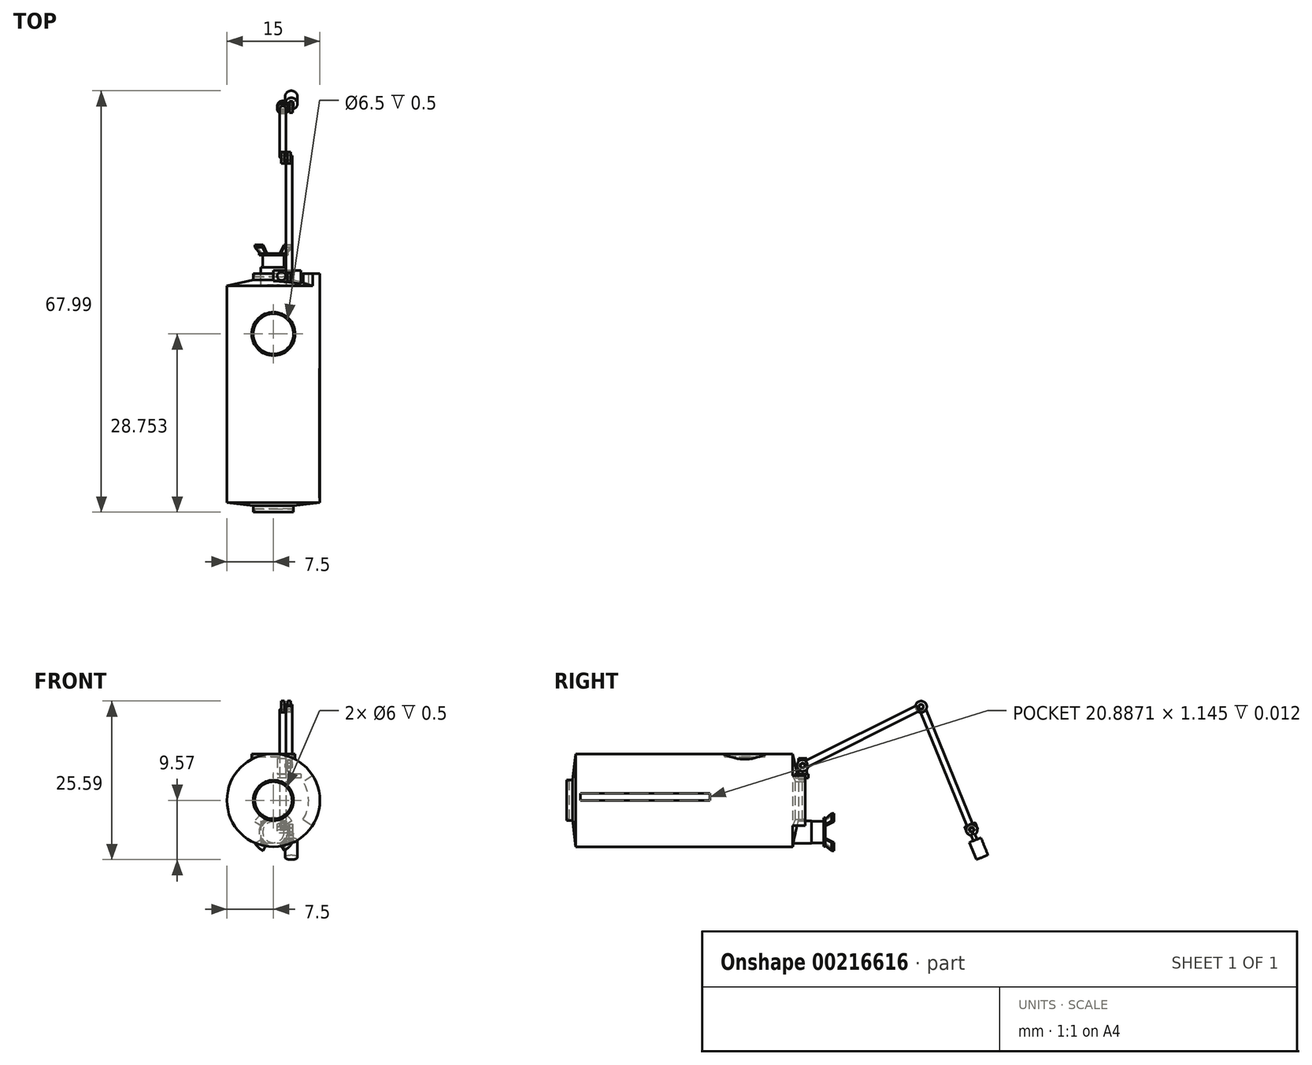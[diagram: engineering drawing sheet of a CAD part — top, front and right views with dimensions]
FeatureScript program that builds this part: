
annotation { "Feature Type Name" : "Feature", "Feature Type Description" : "" }
export const myFeature = defineFeature(function(context is Context, id is Id, definition is map)
    precondition{}
    {
        {
            var Q0;
            Q0=qCreatedBy(makeId("Front.planeOp"),FACE);
            var sketch = newSketch(context, id + "F0", { "sketchPlane" : qUnion([Q0])});
            skCircle(sketch, "E0", {"center": v(0, 0) * mm, "radius": 3.25 * mm});
            skSolve(sketch);
        }
        {
            var Q0;
            Q0=qCreatedBy(makeId("Front.planeOp"),FACE);
            cPlane(context, id + "F1", {"entities" : qUnion([Q0]), "cplaneType" : CPlaneType.OFFSET, "offset" : .5 * mm, "oppositeDirection" : true, "width" : 150 * mm, "height" : 150 * mm});
        }
        {
            var Q0;
            Q0=qCreatedBy(id+"F1.planeOp",FACE);
            var sketch = newSketch(context, id + "F2", { "sketchPlane" : qUnion([Q0])});
            skCircle(sketch, "E1", {"center": v(0, 0) * mm, "radius": 7.5 * mm});
            skSolve(sketch);
        }
        {
            var Q0;
            Q0=makeQuery(id+"F0.imprint","IMPRINT",FACE,{"disambiguationData":[TD([[makeQuery(id+"F0.imprint","IMPRINT",EDGE,{"derivedFrom":sQuery(id+"F0.wireOp",EDGE,"E0")}),1.0]])]});
            var Q1;
            Q1=makeQuery(id+"F2.imprint","IMPRINT",FACE,{"disambiguationData":[TD([[makeQuery(id+"F2.imprint","IMPRINT",EDGE,{"derivedFrom":sQuery(id+"F2.wireOp",EDGE,"E1")}),1.0]])]});
            loft(context, id + "F3", {"sheetProfilesArray" : [{ "sheetProfileEntities" : qUnion([Q0]) }, { "sheetProfileEntities" : qUnion([Q1]) }]});
        }
        {
            var Q0;
            Q0=makeQuery(id+"F3.opLoft","CAP_FACE",FACE,{"disambiguationData":[OSD([makeQuery(id+"F0.imprint","IMPRINT",FACE,{"disambiguationData":[TD([[makeQuery(id+"F0.imprint","IMPRINT",EDGE,{"derivedFrom":sQuery(id+"F0.wireOp",EDGE,"E0")}),1.0]])]})])],"isStart":true});
            extrude(context, id + "F4", {"entities" : qUnion([Q0]), "operationType" : NewBodyOperationType.ADD, "depth" : 1 * mm});
        }
        {
            var Q0;
            Q0=makeQuery(id+"F4.opExtrude","CAP_FACE",FACE,{"disambiguationData":[OSD([makeQuery(id+"F0.imprint","IMPRINT",FACE,{"disambiguationData":[TD([[makeQuery(id+"F0.imprint","IMPRINT",EDGE,{"derivedFrom":sQuery(id+"F0.wireOp",EDGE,"E0")}),1.0]])]})])],"isStart":false});
            var sketch = newSketch(context, id + "F5", { "sketchPlane" : qUnion([Q0])});
            skCircle(sketch, "E2", {"center": v(0, 0) * mm, "radius": 3 * mm});
            skSolve(sketch);
        }
        {
            var Q0;
            Q0=makeQuery(id+"F5.imprint","IMPRINT",FACE,{"disambiguationData":[TD([[makeQuery(id+"F5.imprint","IMPRINT",EDGE,{"derivedFrom":sQuery(id+"F5.wireOp",EDGE,"E2")}),1.0]])]});
            extrude(context, id + "F6", {"entities" : qUnion([Q0]), "operationType" : NewBodyOperationType.REMOVE, "oppositeDirection" : true, "depth" : .5 * mm});
        }
        {
            var Q0;
            Q0=makeQuery(id+"F3.opLoft","CAP_FACE",FACE,{"disambiguationData":[OSD([makeQuery(id+"F2.imprint","IMPRINT",FACE,{"disambiguationData":[TD([[makeQuery(id+"F2.imprint","IMPRINT",EDGE,{"derivedFrom":sQuery(id+"F2.wireOp",EDGE,"E1")}),1.0]])]})])],"isStart":true});
            extrude(context, id + "F7", {"entities" : qUnion([Q0]), "operationType" : NewBodyOperationType.ADD, "depth" : 35 * mm});
        }
        {
            var Q0;
            Q0=qCreatedBy(makeId("Right.planeOp"),FACE);
            cPlane(context, id + "F8", {"entities" : qUnion([Q0]), "cplaneType" : CPlaneType.OFFSET, "offset" : 7.5 * mm, "width" : 150 * mm, "height" : 150 * mm});
        }
        {
            var Q0;
            Q0=qCreatedBy(id+"F8.planeOp",FACE);
            var sketch = newSketch(context, id + "F9", { "sketchPlane" : qUnion([Q0])});
            skLineSegment(sketch, "E3.bottom", {"start": v(1.27, 0) * mm, "end": v(22.15, 0) * mm});
            skLineSegment(sketch, "E3.top", {"start": v(1.27, 1.15) * mm, "end": v(22.15, 1.15) * mm});
            skLineSegment(sketch, "E3.left", {"start": v(1.27, 0) * mm, "end": v(1.27, 1.15) * mm});
            skLineSegment(sketch, "E3.right", {"start": v(22.15, 0) * mm, "end": v(22.15, 1.15) * mm});
            skSolve(sketch);
        }
        {
            var Q0;
            Q0=makeQuery(id+"F9.imprint","IMPRINT",FACE,{"disambiguationData":[TD([[makeQuery(id+"F9.imprint","IMPRINT",EDGE,{"derivedFrom":sQuery(id+"F9.wireOp",EDGE,"E3.bottom")}),1.0]])]});
            extrude(context, id + "F10", {"entities" : qUnion([Q0]), "operationType" : NewBodyOperationType.REMOVE, "oppositeDirection" : true, "depth" : .1 * mm});
        }
        {
            var Q0;
            Q0=qCreatedBy(id+"F1.planeOp",FACE);
            cPlane(context, id + "F11", {"entities" : qUnion([Q0]), "cplaneType" : CPlaneType.OFFSET, "offset" : 36 * mm, "oppositeDirection" : true, "width" : 150 * mm, "height" : 150 * mm});
        }
        {
            var Q0;
            Q0=qCreatedBy(id+"F11.planeOp",FACE);
            var sketch = newSketch(context, id + "F12", { "sketchPlane" : qUnion([Q0])});
            skCircle(sketch, "E4", {"center": v(0, 0) * mm, "radius": 3.25 * mm});
            skSolve(sketch);
        }
        {
            var Q1;
            Q1=makeQuery(id+"F7.opExtrude","CAP_FACE",FACE,{"disambiguationData":[OSD([makeQuery(id+"F2.imprint","IMPRINT",FACE,{"disambiguationData":[TD([[makeQuery(id+"F2.imprint","IMPRINT",EDGE,{"derivedFrom":sQuery(id+"F2.wireOp",EDGE,"E1")}),1.0]])]})])],"isStart":false});
            var Q2;
            Q2=makeQuery(id+"F12.imprint","IMPRINT",FACE,{"disambiguationData":[TD([[makeQuery(id+"F12.imprint","IMPRINT",EDGE,{"derivedFrom":sQuery(id+"F12.wireOp",EDGE,"E4")}),1.0]])]});
            loft(context, id + "F13", {"operationType" : NewBodyOperationType.ADD, "sheetProfilesArray" : [{ "sheetProfileEntities" : qUnion([Q1]) }, { "sheetProfileEntities" : qUnion([Q2]) }]});
        }
        {
            var Q0;
            Q0=makeQuery(id+"F13.opLoft","CAP_FACE",FACE,{"disambiguationData":[OSD([makeQuery(id+"F12.imprint","IMPRINT",FACE,{"disambiguationData":[TD([[makeQuery(id+"F12.imprint","IMPRINT",EDGE,{"derivedFrom":sQuery(id+"F12.wireOp",EDGE,"E4")}),1.0]])]})])],"isStart":true});
            extrude(context, id + "F14", {"entities" : qUnion([Q0]), "operationType" : NewBodyOperationType.ADD, "depth" : 1 * mm});
        }
        {
            var Q0;
            Q0=qCreatedBy(id+"F11.planeOp",FACE);
            var sketch = newSketch(context, id + "F15", { "sketchPlane" : qUnion([Q0])});
            skLineSegment(sketch, "E5", {"start": v(0, 0) * mm, "end": v(0, -7.48) * mm});
            skLineSegment(sketch, "E6", {"start": v(0, -7.48) * mm, "end": v(0, -3.26) * mm});
            skLineSegment(sketch, "E7.bottom", {"start": v(2.05, -3.32) * mm, "end": v(-2.05, -3.32) * mm});
            skLineSegment(sketch, "E7.top", {"start": v(2.05, -6.95) * mm, "end": v(-2.05, -6.95) * mm});
            skLineSegment(sketch, "E7.left", {"start": v(2.05, -3.32) * mm, "end": v(2.05, -6.95) * mm});
            skLineSegment(sketch, "E7.right", {"start": v(-2.05, -3.32) * mm, "end": v(-2.05, -6.95) * mm});
            skPoint(sketch, "E7.middle", {"position": v(0, -5.13) * mm});
            skSolve(sketch);
        }
        {
            var Q0;
            {var subQ5=sQuery(id+"F15.wireOp",EDGE,"E7.left");Q0=makeQuery(id+"F15.imprint","IMPRINT",FACE,{"disambiguationData":[TD([[makeQuery(id+"F15.imprint","IMPRINT",EDGE,{"derivedFrom":subQ5}),-1.0]])]});}
            var Q1;
            {var subQ5=sQuery(id+"F15.wireOp",EDGE,"E7.right");Q1=makeQuery(id+"F15.imprint","IMPRINT",FACE,{"disambiguationData":[TD([[makeQuery(id+"F15.imprint","IMPRINT",EDGE,{"derivedFrom":subQ5}),1.0]])]});}
            extrude(context, id + "F16", {"entities" : qUnion([Q0, Q1]), "operationType" : NewBodyOperationType.ADD, "depth" : 3 * mm, "hasSecondDirection" : true, "secondDirectionOppositeDirection" : true, "secondDirectionDepth" : 2 * mm});
        }
        {
            var Q0;
            Q0=qCreatedBy(id+"F11.planeOp",FACE);
            var sketch = newSketch(context, id + "F17", { "sketchPlane" : qUnion([Q0])});
            skCircle(sketch, "E8", {"center": v(0, 0) * mm, "radius": 7.5 * mm});
            skLineSegment(sketch, "E9", {"start": v(4.81, 3) * mm, "end": v(6.36, 3.97) * mm});
            skLineSegment(sketch, "E10", {"start": v(6.3, -4.05) * mm, "end": v(4.78, -3.07) * mm});
            skArc(sketch, "E11", {"start": v(4.78, -3.07) * mm, "mid": v(5.68, -0.04) * mm, "end": v(4.81, 3) * mm});
            skSolve(sketch);
        }
        {
            var Q0;
            {var subQ0=sQuery(id+"F17.wireOp",EDGE,"E9");Q0=makeQuery(id+"F17.imprint","IMPRINT",FACE,{"disambiguationData":[TD([[makeQuery(id+"F17.imprint","IMPRINT",EDGE,{"derivedFrom":subQ0}),-1.0]])]});}
            extrude(context, id + "F18", {"entities" : qUnion([Q0]), "operationType" : NewBodyOperationType.ADD, "depth" : 2 * mm, "hasSecondDirection" : true, "secondDirectionOppositeDirection" : true, "secondDirectionDepth" : 1 * mm});
        }
        {
            var Q0;
            Q0=qCreatedBy(id+"F11.planeOp",FACE);
            var sketch = newSketch(context, id + "F19", { "sketchPlane" : qUnion([Q0])});
            skLineSegment(sketch, "E12.bottom", {"start": v(4.44, 4.25) * mm, "end": v(0, 4.25) * mm});
            skLineSegment(sketch, "E12.top", {"start": v(4.44, 3.61) * mm, "end": v(0, 3.61) * mm});
            skLineSegment(sketch, "E12.left", {"start": v(4.44, 4.25) * mm, "end": v(4.44, 3.61) * mm});
            skLineSegment(sketch, "E12.right", {"start": v(0, 4.25) * mm, "end": v(0, 3.61) * mm});
            skSolve(sketch);
        }
        {
            var Q0;
            Q0=makeQuery(id+"F19.imprint","IMPRINT",FACE,{"disambiguationData":[TD([[makeQuery(id+"F19.imprint","IMPRINT",EDGE,{"derivedFrom":sQuery(id+"F19.wireOp",EDGE,"E12.bottom")}),1.0]])]});
            extrude(context, id + "F20", {"entities" : qUnion([Q0]), "operationType" : NewBodyOperationType.ADD, "depth" : 2 * mm, "hasSecondDirection" : true, "secondDirectionOppositeDirection" : true, "secondDirectionDepth" : 1.5 * mm});
        }
        {
            var Q0;
            Q0=makeQuery(id+"F20.opExtrude","SWEPT_FACE",FACE,{"disambiguationData":[OSD([sQuery(id+"F19.wireOp",EDGE,"E12.bottom")])]});
            var sketch = newSketch(context, id + "F21", { "sketchPlane" : qUnion([Q0])});
            skCircle(sketch, "E13", {"center": v(1.29, 37.08) * mm, "radius": 0.67 * mm});
            skSolve(sketch);
        }
        {
            var Q0;
            Q0=makeQuery(id+"F21.imprint","IMPRINT",FACE,{"disambiguationData":[TD([[makeQuery(id+"F21.imprint","IMPRINT",EDGE,{"derivedFrom":sQuery(id+"F21.wireOp",EDGE,"E13")}),1.0]])]});
            extrude(context, id + "F22", {"entities" : qUnion([Q0]), "operationType" : NewBodyOperationType.ADD, "depth" : 2.5 * mm});
        }
        {
            var Q0;
            Q0=qCreatedBy(makeId("Right.planeOp"),FACE);
            cPlane(context, id + "F23", {"entities" : qUnion([Q0]), "cplaneType" : CPlaneType.OFFSET, "offset" : 2 * mm, "width" : 150 * mm, "height" : 150 * mm});
        }
        {
            var Q0;
            Q0=qCreatedBy(id+"F23.planeOp",FACE);
            var sketch = newSketch(context, id + "F24", { "sketchPlane" : qUnion([Q0])});
            skCircle(sketch, "E14", {"center": v(37.1, 5.6) * mm, "radius": 0.33 * mm});
            skSolve(sketch);
        }
        {
            var Q0;
            Q0=makeQuery(id+"F24.imprint","IMPRINT",FACE,{"disambiguationData":[TD([[makeQuery(id+"F24.imprint","IMPRINT",EDGE,{"derivedFrom":sQuery(id+"F24.wireOp",EDGE,"E14")}),1.0]])]});
            extrude(context, id + "F25", {"entities" : qUnion([Q0]), "operationType" : NewBodyOperationType.ADD, "depth" : 1 * mm, "hasSecondDirection" : true, "secondDirectionOppositeDirection" : true, "secondDirectionDepth" : 1 * mm});
        }
        {
            var Q0;
            Q0=qCreatedBy(id+"F23.planeOp",FACE);
            cPlane(context, id + "F26", {"entities" : qUnion([Q0]), "cplaneType" : CPlaneType.OFFSET, "offset" : .5 * mm, "width" : 150 * mm, "height" : 150 * mm});
        }
        {
            var Q0;
            Q0=qCreatedBy(id+"F26.planeOp",FACE);
            var sketch = newSketch(context, id + "F27", { "sketchPlane" : qUnion([Q0])});
            skCircle(sketch, "E15", {"center": v(37.1, 5.61) * mm, "radius": 0.92 * mm});
            skCircle(sketch, "E16", {"center": v(37.1, 5.61) * mm, "radius": 0.4 * mm});
            skSolve(sketch);
        }
        {
            var Q0;
            Q0=makeQuery(id+"F27.imprint","IMPRINT",FACE,{"disambiguationData":[TD([[makeQuery(id+"F27.imprint","IMPRINT",EDGE,{"derivedFrom":sQuery(id+"F27.wireOp",EDGE,"E15")}),1.0]])]});
            extrude(context, id + "F28", {"entities" : qUnion([Q0]), "depth" : .25 * mm, "hasSecondDirection" : true, "secondDirectionOppositeDirection" : true, "secondDirectionDepth" : .25 * mm});
        }
        {
            var Q0;
            Q0=qCreatedBy(id+"F26.planeOp",FACE);
            var sketch = newSketch(context, id + "F29", { "sketchPlane" : qUnion([Q0])});
            skLineSegment(sketch, "E17", {"start": v(37.13, 5.58) * mm, "end": v(37.8, 5.91) * mm});
            skLineSegment(sketch, "E18", {"start": v(37.8, 5.91) * mm, "end": v(37.57, 6.36) * mm});
            skLineSegment(sketch, "E19", {"start": v(37.8, 5.91) * mm, "end": v(38.01, 5.47) * mm});
            skLineSegment(sketch, "E20", {"start": v(37.57, 6.36) * mm, "end": v(55.46, 15.3) * mm});
            skLineSegment(sketch, "E21", {"start": v(38.01, 5.47) * mm, "end": v(55.9, 14.41) * mm});
            skLineSegment(sketch, "E22", {"start": v(55.9, 14.41) * mm, "end": v(55.46, 15.3) * mm});
            skSolve(sketch);
        }
        {
            var Q0;
            Q0=makeQuery(id+"F29.imprint","IMPRINT",FACE,{"disambiguationData":[TD([[makeQuery(id+"F29.imprint","IMPRINT",EDGE,{"derivedFrom":sQuery(id+"F29.wireOp",EDGE,"E18")}),-1.0]])]});
            extrude(context, id + "F30", {"entities" : qUnion([Q0]), "operationType" : NewBodyOperationType.ADD, "oppositeDirection" : true, "depth" : .5 * mm, "hasSecondDirection" : true, "secondDirectionOppositeDirection" : false, "secondDirectionDepth" : .5 * mm});
        }
        {
            var Q0;
            Q0=makeQuery(id+"F30.opExtrude","CAP_EDGE",EDGE,{"disambiguationData":[OSD([sQuery(id+"F29.wireOp",EDGE,"E20")])],"isStart":true});
            var Q1;
            Q1=makeQuery(id+"F30.opExtrude","CAP_EDGE",EDGE,{"disambiguationData":[OSD([sQuery(id+"F29.wireOp",EDGE,"E21")])],"isStart":true});
            var Q2;
            Q2=makeQuery(id+"F30.opExtrude","CAP_EDGE",EDGE,{"disambiguationData":[OSD([sQuery(id+"F29.wireOp",EDGE,"E20")])],"isStart":false});
            var Q3;
            Q3=makeQuery(id+"F30.opExtrude","CAP_EDGE",EDGE,{"disambiguationData":[OSD([sQuery(id+"F29.wireOp",EDGE,"E21")])],"isStart":false});
            fillet(context, id + "F31", {"entities" : qUnion([Q0, Q1, Q2, Q3]), "radius" : .3 * mm, "tangentPropagation" : true, "allowEdgeOverflow" : false});
        }
        {
            var Q0;
            Q0=qCreatedBy(id+"F26.planeOp",FACE);
            var sketch = newSketch(context, id + "F32", { "sketchPlane" : qUnion([Q0])});
            skCircle(sketch, "E23", {"center": v(56.2, 15.1) * mm, "radius": 0.92 * mm});
            skCircle(sketch, "E24", {"center": v(56.2, 15.1) * mm, "radius": 0.4 * mm});
            skSolve(sketch);
        }
        {
            var Q0;
            Q0=makeQuery(id+"F32.imprint","IMPRINT",FACE,{"disambiguationData":[TD([[makeQuery(id+"F32.imprint","IMPRINT",EDGE,{"derivedFrom":sQuery(id+"F32.wireOp",EDGE,"E23")}),1.0]])]});
            extrude(context, id + "F33", {"entities" : qUnion([Q0]), "operationType" : NewBodyOperationType.ADD, "depth" : .25 * mm, "hasSecondDirection" : true, "secondDirectionOppositeDirection" : true, "secondDirectionDepth" : .25 * mm});
        }
        {
            var Q0;
            Q0=qCreatedBy(id+"F23.planeOp",FACE);
            var sketch = newSketch(context, id + "F34", { "sketchPlane" : qUnion([Q0])});
            skLineSegment(sketch, "E25", {"start": v(55.8, 15.1) * mm, "end": v(56.6, 15.1) * mm});
            skLineSegment(sketch, "E26", {"start": v(56.2, 15.5) * mm, "end": v(56.2, 14.7) * mm});
            skCircle(sketch, "E27", {"center": v(56.2, 15.1) * mm, "radius": 0.36 * mm});
            skSolve(sketch);
        }
        {
            var Q0;
            {var subQ0=sQuery(id+"F34.wireOp",EDGE,"E27");var subQ1=sQuery(id+"F34.wireOp",EDGE,"E25");var subQ2=makeQuery(id+"F34.imprint","INTERSECT",VERTEX,{"disambiguationData":[OD(1.0)],"derivedFrom":[subQ1,subQ0]});Q0=makeQuery(id+"F34.imprint","IMPRINT",FACE,{"disambiguationData":[TD([[makeQuery(id+"F34.imprint","IMPRINT",EDGE,{"disambiguationData":[TD([[subQ2,1.0]])],"derivedFrom":subQ1}),-1.0]])]});}
            var Q1;
            {var subQ0=sQuery(id+"F34.wireOp",EDGE,"E27");var subQ1=sQuery(id+"F34.wireOp",EDGE,"E25");var subQ2=makeQuery(id+"F34.imprint","INTERSECT",VERTEX,{"disambiguationData":[OD(0.0)],"derivedFrom":[subQ1,subQ0]});Q1=makeQuery(id+"F34.imprint","IMPRINT",FACE,{"disambiguationData":[TD([[makeQuery(id+"F34.imprint","IMPRINT",EDGE,{"disambiguationData":[TD([[subQ2,-1.0]])],"derivedFrom":subQ1}),-1.0]])]});}
            var Q2;
            {var subQ0=sQuery(id+"F34.wireOp",EDGE,"E27");var subQ1=sQuery(id+"F34.wireOp",EDGE,"E25");var subQ2=makeQuery(id+"F34.imprint","INTERSECT",VERTEX,{"disambiguationData":[OD(1.0)],"derivedFrom":[subQ1,subQ0]});Q2=makeQuery(id+"F34.imprint","IMPRINT",FACE,{"disambiguationData":[TD([[makeQuery(id+"F34.imprint","IMPRINT",EDGE,{"disambiguationData":[TD([[subQ2,1.0]])],"derivedFrom":subQ1}),1.0]])]});}
            var Q3;
            {var subQ0=sQuery(id+"F34.wireOp",EDGE,"E27");var subQ1=sQuery(id+"F34.wireOp",EDGE,"E25");var subQ2=makeQuery(id+"F34.imprint","INTERSECT",VERTEX,{"disambiguationData":[OD(0.0)],"derivedFrom":[subQ1,subQ0]});Q3=makeQuery(id+"F34.imprint","IMPRINT",FACE,{"disambiguationData":[TD([[makeQuery(id+"F34.imprint","IMPRINT",EDGE,{"disambiguationData":[TD([[subQ2,-1.0]])],"derivedFrom":subQ1}),1.0]])]});}
            extrude(context, id + "F35", {"entities" : qUnion([Q0, Q1, Q2, Q3]), "depth" : 1 * mm, "hasSecondDirection" : true, "secondDirectionOppositeDirection" : true, "secondDirectionDepth" : .25 * mm});
        }
        {
            var Q0;
            Q0=makeQuery(id+"F35.opExtrude","CAP_FACE",FACE,{"disambiguationData":[OSD([sQuery(id+"F34.wireOp",EDGE,"E27")])],"isStart":true});
            var sketch = newSketch(context, id + "F36", { "sketchPlane" : qUnion([Q0])});
            skCircle(sketch, "E28", {"center": v(-56.2, 15.1) * mm, "radius": 0.92 * mm});
            skSolve(sketch);
        }
        {
            var Q0;
            Q0=makeQuery(id+"F36.imprint","IMPRINT",FACE,{"disambiguationData":[TD([[makeQuery(id+"F36.imprint","IMPRINT",EDGE,{"derivedFrom":sQuery(id+"F36.wireOp",EDGE,"E28")}),1.0]])]});
            extrude(context, id + "F37", {"entities" : qUnion([Q0]), "operationType" : NewBodyOperationType.ADD, "depth" : .5 * mm});
        }
        {
            var Q0;
            Q0=makeQuery(id+"F35.opExtrude","CAP_FACE",FACE,{"disambiguationData":[OSD([sQuery(id+"F34.wireOp",EDGE,"E27")])],"isStart":true});
            extrude(context, id + "F38", {"entities" : qUnion([Q0]), "depth" : .5 * mm});
        }
        {
            var Q0;
            Q0=qCreatedBy(id+"F23.planeOp",FACE);
            cPlane(context, id + "F39", {"entities" : qUnion([Q0]), "cplaneType" : CPlaneType.OFFSET, "offset" : .5 * mm, "oppositeDirection" : true, "width" : 150 * mm, "height" : 150 * mm});
        }
        {
            var Q0;
            Q0=qCreatedBy(id+"F39.planeOp",FACE);
            var sketch = newSketch(context, id + "F40", { "sketchPlane" : qUnion([Q0])});
            skLineSegment(sketch, "E29", {"start": v(56.49, 14.55) * mm, "end": v(56.95, 14.74) * mm});
            skLineSegment(sketch, "E30", {"start": v(56.95, 14.74) * mm, "end": v(56.03, 14.36) * mm});
            skLineSegment(sketch, "E31", {"start": v(56.95, 14.74) * mm, "end": v(64.51, -3.78) * mm});
            skLineSegment(sketch, "E32", {"start": v(56.03, 14.36) * mm, "end": v(63.58, -4.15) * mm});
            skLineSegment(sketch, "E33", {"start": v(64.51, -3.78) * mm, "end": v(63.58, -4.15) * mm});
            skSolve(sketch);
        }
        {
            var Q0;
            {var subQ0=sQuery(id+"F40.wireOp",EDGE,"E31");Q0=makeQuery(id+"F40.imprint","IMPRINT",FACE,{"disambiguationData":[TD([[makeQuery(id+"F40.imprint","IMPRINT",EDGE,{"derivedFrom":subQ0}),-1.0]])]});}
            extrude(context, id + "F41", {"entities" : qUnion([Q0]), "operationType" : NewBodyOperationType.ADD, "depth" : .5 * mm, "hasSecondDirection" : true, "secondDirectionOppositeDirection" : true, "secondDirectionDepth" : .5 * mm});
        }
        {
            var Q0;
            Q0=makeQuery(id+"F41.opExtrude","CAP_EDGE",EDGE,{"disambiguationData":[OSD([sQuery(id+"F40.wireOp",EDGE,"E31")])],"isStart":true});
            var Q1;
            Q1=makeQuery(id+"F41.opExtrude","CAP_EDGE",EDGE,{"disambiguationData":[OSD([sQuery(id+"F40.wireOp",EDGE,"E32")])],"isStart":true});
            var Q2;
            Q2=makeQuery(id+"F41.opExtrude","CAP_EDGE",EDGE,{"disambiguationData":[OSD([sQuery(id+"F40.wireOp",EDGE,"E31")])],"isStart":false});
            var Q3;
            Q3=makeQuery(id+"F41.opExtrude","CAP_EDGE",EDGE,{"disambiguationData":[OSD([sQuery(id+"F40.wireOp",EDGE,"E32")])],"isStart":false});
            fillet(context, id + "F42", {"entities" : qUnion([Q0, Q1, Q2, Q3]), "radius" : .4 * mm, "tangentPropagation" : true, "allowEdgeOverflow" : false});
        }
        {
            var Q0;
            Q0=makeQuery(id+"F41.opExtrude","SWEPT_FACE",FACE,{"disambiguationData":[OSD([sQuery(id+"F40.wireOp",EDGE,"E33")])]});
            var sketch = newSketch(context, id + "F43", { "sketchPlane" : qUnion([Q0])});
            skCircle(sketch, "E34", {"center": v(1.51, -57.85) * mm, "radius": 0.92 * mm});
            skSolve(sketch);
        }
        {
            var Q0;
            Q0=makeQuery(id+"F43.imprint","IMPRINT",FACE,{"disambiguationData":[TD([[makeQuery(id+"F43.imprint","IMPRINT",EDGE,{"derivedFrom":sQuery(id+"F43.wireOp",EDGE,"E34")}),1.0]])]});
            var Q1;
            {var subQ0=sQuery(id+"F40.wireOp",EDGE,"E33");Q1=makeQuery(id+"F43.imprint","IMPRINT",FACE,{"disambiguationData":[TD([[makeQuery(id+"F43.imprint","IMPRINT",EDGE,{"derivedFrom":makeQuery(id+"F41.opExtrude","CAP_EDGE",EDGE,{"disambiguationData":[OSD([subQ0])],"isStart":true})}),-1.0]])]});}
            extrude(context, id + "F44", {"entities" : qUnion([Q0, Q1]), "operationType" : NewBodyOperationType.ADD, "depth" : .5 * mm});
        }
        {
            var Q0;
            Q0=makeQuery(id+"F44.opExtrude","CAP_FACE",FACE,{"disambiguationData":[OSD([sQuery(id+"F43.wireOp",EDGE,"E34")])],"isStart":false});
            var sketch = newSketch(context, id + "F45", { "sketchPlane" : qUnion([Q0])});
            skCircle(sketch, "E35", {"center": v(1.51, -57.85) * mm, "radius": 0.37 * mm});
            skSolve(sketch);
        }
        {
            var Q0;
            Q0=makeQuery(id+"F45.imprint","IMPRINT",FACE,{"disambiguationData":[TD([[makeQuery(id+"F45.imprint","IMPRINT",EDGE,{"derivedFrom":sQuery(id+"F45.wireOp",EDGE,"E35")}),1.0]])]});
            extrude(context, id + "F46", {"entities" : qUnion([Q0]), "operationType" : NewBodyOperationType.REMOVE, "oppositeDirection" : true, "depth" : .25 * mm});
        }
        {
            var Q0;
            Q0=makeQuery(id+"F44.opExtrude","CAP_FACE",FACE,{"disambiguationData":[OSD([sQuery(id+"F43.wireOp",EDGE,"E34")])],"isStart":false});
            cPlane(context, id + "F47", {"entities" : qUnion([Q0]), "cplaneType" : CPlaneType.OFFSET, "offset" : .1 * mm, "width" : 150 * mm, "height" : 150 * mm});
        }
        {
            var Q0;
            Q0=qCreatedBy(id+"F47.planeOp",FACE);
            var sketch = newSketch(context, id + "F48", { "sketchPlane" : qUnion([Q0])});
            skLineSegment(sketch, "E36", {"start": v(1.5, -57.81) * mm, "end": v(1.5, -57.84) * mm});
            skCircle(sketch, "E37", {"center": v(1.5, -57.84) * mm, "radius": 0.33 * mm});
            skSolve(sketch);
        }
        {
            var Q0;
            Q0 = qSketchRegion(id + "F48", true);
            extrude(context, id + "F49", {"entities" : qUnion([Q0]), "oppositeDirection" : true, "depth" : .3 * mm});
        }
        {
            var Q0;
            Q0=makeQuery(id+"F49.opExtrude","CAP_FACE",FACE,{"disambiguationData":[OSD([sQuery(id+"F48.wireOp",EDGE,"E37")])],"isStart":true});
            var sketch = newSketch(context, id + "F50", { "sketchPlane" : qUnion([Q0])});
            skCircle(sketch, "E38", {"center": v(1.5, -57.84) * mm, "radius": 0.92 * mm});
            skSolve(sketch);
        }
        {
            var Q0;
            Q0=makeQuery(id+"F50.imprint","IMPRINT",FACE,{"disambiguationData":[TD([[makeQuery(id+"F50.imprint","IMPRINT",EDGE,{"derivedFrom":sQuery(id+"F50.wireOp",EDGE,"E38")}),1.0]])]});
            var Q1;
            Q1=makeQuery(id+"F50.imprint","IMPRINT",FACE,{"disambiguationData":[TD([[makeQuery(id+"F50.imprint","IMPRINT",EDGE,{"derivedFrom":makeQuery(id+"F49.opExtrude","CAP_EDGE",EDGE,{"disambiguationData":[OSD([sQuery(id+"F48.wireOp",EDGE,"E37")])],"isStart":true})}),1.0]])]});
            extrude(context, id + "F51", {"entities" : qUnion([Q0, Q1]), "operationType" : NewBodyOperationType.ADD, "depth" : .5 * mm});
        }
        {
            var Q0;
            Q0=qCreatedBy(id+"F26.planeOp",FACE);
            var sketch = newSketch(context, id + "F52", { "sketchPlane" : qUnion([Q0])});
            skLineSegment(sketch, "E39", {"start": v(64.27, -4.53) * mm, "end": v(64.46, -4.99) * mm});
            skCircle(sketch, "E40", {"center": v(64.36, -4.76) * mm, "radius": 0.92 * mm});
            skCircle(sketch, "E41", {"center": v(64.36, -4.76) * mm, "radius": 0.3 * mm});
            skSolve(sketch);
        }
        {
            var Q0;
            Q0=makeQuery(id+"F52.imprint","IMPRINT",FACE,{"disambiguationData":[TD([[makeQuery(id+"F52.imprint","IMPRINT",EDGE,{"derivedFrom":sQuery(id+"F52.wireOp",EDGE,"E41")}),1.0]])]});
            extrude(context, id + "F53", {"entities" : qUnion([Q0]), "operationType" : NewBodyOperationType.ADD, "oppositeDirection" : true, "depth" : .1 * mm, "hasSecondDirection" : true, "secondDirectionOppositeDirection" : false, "secondDirectionDepth" : .6 * mm});
        }
        {
            var Q0;
            Q0=makeQuery(id+"F53.opExtrude","CAP_FACE",FACE,{"disambiguationData":[OSD([sQuery(id+"F52.wireOp",EDGE,"E41")])],"isStart":true});
            var sketch = newSketch(context, id + "F54", { "sketchPlane" : qUnion([Q0])});
            skCircle(sketch, "E42", {"center": v(64.36, -4.76) * mm, "radius": 0.37 * mm});
            skCircle(sketch, "E43", {"center": v(64.36, -4.76) * mm, "radius": 0.92 * mm});
            skSolve(sketch);
        }
        {
            var Q0;
            Q0=makeQuery(id+"F54.imprint","IMPRINT",FACE,{"disambiguationData":[TD([[makeQuery(id+"F54.imprint","IMPRINT",EDGE,{"derivedFrom":sQuery(id+"F54.wireOp",EDGE,"E42")}),-1.0]])]});
            extrude(context, id + "F55", {"entities" : qUnion([Q0]), "oppositeDirection" : true, "depth" : .5 * mm});
        }
        {
            var Q0;
            Q0=qCreatedBy(id+"F47.planeOp",FACE);
            cPlane(context, id + "F56", {"entities" : qUnion([Q0]), "cplaneType" : CPlaneType.OFFSET, "offset" : 1 * mm, "width" : 150 * mm, "height" : 150 * mm});
        }
        {
            var Q0;
            Q0=qCreatedBy(id+"F56.planeOp",FACE);
            var sketch = newSketch(context, id + "F57", { "sketchPlane" : qUnion([Q0])});
            skCircle(sketch, "E44", {"center": v(2.88, -57.7) * mm, "radius": 0.32 * mm});
            skSolve(sketch);
        }
        {
            var Q0;
            Q0=makeQuery(id+"F57.imprint","IMPRINT",FACE,{"disambiguationData":[TD([[makeQuery(id+"F57.imprint","IMPRINT",EDGE,{"derivedFrom":sQuery(id+"F57.wireOp",EDGE,"E44")}),1.0]])]});
            extrude(context, id + "F58", {"entities" : qUnion([Q0]), "operationType" : NewBodyOperationType.ADD, "depth" : 1 * mm, "hasSecondDirection" : true, "secondDirectionOppositeDirection" : true, "secondDirectionDepth" : .1 * mm});
        }
        {
            var Q0;
            Q0=makeQuery(id+"F58.opExtrude","CAP_FACE",FACE,{"disambiguationData":[OSD([sQuery(id+"F57.wireOp",EDGE,"E44")])],"isStart":false});
            var sketch = newSketch(context, id + "F59", { "sketchPlane" : qUnion([Q0])});
            skCircle(sketch, "E45", {"center": v(2.88, -57.7) * mm, "radius": 1 * mm});
            skSolve(sketch);
        }
        {
            var Q0;
            Q0=makeQuery(id+"F59.imprint","IMPRINT",FACE,{"disambiguationData":[TD([[makeQuery(id+"F59.imprint","IMPRINT",EDGE,{"derivedFrom":sQuery(id+"F59.wireOp",EDGE,"E45")}),1.0]])]});
            var Q1;
            Q1=makeQuery(id+"F59.imprint","IMPRINT",FACE,{"disambiguationData":[TD([[makeQuery(id+"F59.imprint","IMPRINT",EDGE,{"derivedFrom":makeQuery(id+"F58.opExtrude","CAP_EDGE",EDGE,{"disambiguationData":[OSD([sQuery(id+"F57.wireOp",EDGE,"E44")])],"isStart":false})}),1.0]])]});
            extrude(context, id + "F60", {"entities" : qUnion([Q0, Q1]), "operationType" : NewBodyOperationType.ADD, "depth" : 3 * mm});
        }
        {
            var Q0;
            Q0=makeQuery(id+"F16.opExtrude","CAP_FACE",FACE,{"disambiguationData":[OSD([sQuery(id+"F15.wireOp",EDGE,"E7.bottom"),sQuery(id+"F15.wireOp",EDGE,"E7.top"),sQuery(id+"F15.wireOp",EDGE,"E7.left"),sQuery(id+"F15.wireOp",EDGE,"E7.right")])],"isStart":true});
            var sketch = newSketch(context, id + "F61", { "sketchPlane" : qUnion([Q0])});
            skLineSegment(sketch, "E46", {"start": v(0, -3.32) * mm, "end": v(0, -6.95) * mm});
            skCircle(sketch, "E47", {"center": v(0, -5.13) * mm, "radius": 1.72 * mm});
            skSolve(sketch);
        }
        {
            var Q0;
            {var subQ0=sQuery(id+"F61.wireOp",EDGE,"E47");var subQ1=sQuery(id+"F61.wireOp",EDGE,"E46");var subQ2=makeQuery(id+"F61.imprint","INTERSECT",VERTEX,{"disambiguationData":[OD(0.0)],"derivedFrom":[subQ1,subQ0]});Q0=makeQuery(id+"F61.imprint","IMPRINT",FACE,{"disambiguationData":[TD([[makeQuery(id+"F61.imprint","IMPRINT",EDGE,{"disambiguationData":[TD([[subQ2,-1.0]])],"derivedFrom":subQ1}),1.0]])]});}
            var Q1;
            {var subQ0=sQuery(id+"F61.wireOp",EDGE,"E47");var subQ1=sQuery(id+"F61.wireOp",EDGE,"E46");var subQ2=makeQuery(id+"F61.imprint","INTERSECT",VERTEX,{"disambiguationData":[OD(0.0)],"derivedFrom":[subQ1,subQ0]});Q1=makeQuery(id+"F61.imprint","IMPRINT",FACE,{"disambiguationData":[TD([[makeQuery(id+"F61.imprint","IMPRINT",EDGE,{"disambiguationData":[TD([[subQ2,-1.0]])],"derivedFrom":subQ1}),-1.0]])]});}
            extrude(context, id + "F62", {"entities" : qUnion([Q0, Q1]), "operationType" : NewBodyOperationType.ADD, "depth" : 2 * mm});
        }
        {
            var Q0;
            Q0=makeQuery(id+"F62.opExtrude","CAP_FACE",FACE,{"disambiguationData":[OSD([sQuery(id+"F61.wireOp",EDGE,"E47")])],"isStart":false});
            var sketch = newSketch(context, id + "F63", { "sketchPlane" : qUnion([Q0])});
            skCircle(sketch, "E48", {"center": v(0, -5.13) * mm, "radius": 2.32 * mm});
            skSolve(sketch);
        }
        {
            var Q0;
            Q0=makeQuery(id+"F63.imprint","IMPRINT",FACE,{"disambiguationData":[TD([[makeQuery(id+"F63.imprint","IMPRINT",EDGE,{"derivedFrom":sQuery(id+"F63.wireOp",EDGE,"E48")}),1.0]])]});
            var Q1;
            Q1=makeQuery(id+"F63.imprint","IMPRINT",FACE,{"disambiguationData":[TD([[makeQuery(id+"F63.imprint","IMPRINT",EDGE,{"derivedFrom":makeQuery(id+"F62.opExtrude","CAP_EDGE",EDGE,{"disambiguationData":[OSD([sQuery(id+"F61.wireOp",EDGE,"E47")])],"isStart":false})}),1.0]])]});
            extrude(context, id + "F64", {"entities" : qUnion([Q0, Q1]), "operationType" : NewBodyOperationType.ADD, "depth" : .25 * mm});
        }
        {
            var Q0;
            Q0=makeQuery(id+"F64.opExtrude","CAP_FACE",FACE,{"disambiguationData":[OSD([sQuery(id+"F63.wireOp",EDGE,"E48")])],"isStart":false});
            var sketch = newSketch(context, id + "F65", { "sketchPlane" : qUnion([Q0])});
            skArc(sketch, "E49", {"start": v(1.82, -4.12) * mm, "mid": v(1.5, -3.69) * mm, "end": v(1.07, -3.35) * mm});
            skLineSegment(sketch, "E50", {"start": v(1.07, -3.35) * mm, "end": v(1.78, -2.16) * mm});
            skArc(sketch, "E51", {"start": v(3.03, -3.45) * mm, "mid": v(2.5, -2.72) * mm, "end": v(1.78, -2.16) * mm});
            skLineSegment(sketch, "E52", {"start": v(1.82, -4.12) * mm, "end": v(3.03, -3.45) * mm});
            skArc(sketch, "E53.1.0", {"start": v(-1.01, -3.32) * mm, "mid": v(-1.45, -3.64) * mm, "end": v(-1.78, -4.06) * mm});
            skLineSegment(sketch, "E53.1.1", {"start": v(-1.78, -4.06) * mm, "end": v(-2.97, -3.35) * mm});
            skArc(sketch, "E53.1.2", {"start": v(-1.68, -2.1) * mm, "mid": v(-2.41, -2.64) * mm, "end": v(-2.97, -3.35) * mm});
            skLineSegment(sketch, "E53.1.3", {"start": v(-1.01, -3.32) * mm, "end": v(-1.68, -2.1) * mm});
            skArc(sketch, "E53.2.0", {"start": v(-1.82, -6.14) * mm, "mid": v(-1.5, -6.58) * mm, "end": v(-1.07, -6.92) * mm});
            skLineSegment(sketch, "E53.2.1", {"start": v(-1.07, -6.92) * mm, "end": v(-1.78, -8.1) * mm});
            skArc(sketch, "E53.2.2", {"start": v(-3.03, -6.82) * mm, "mid": v(-2.5, -7.55) * mm, "end": v(-1.78, -8.1) * mm});
            skLineSegment(sketch, "E53.2.3", {"start": v(-1.82, -6.14) * mm, "end": v(-3.03, -6.82) * mm});
            skArc(sketch, "E53.3.0", {"start": v(1.01, -6.95) * mm, "mid": v(1.45, -6.63) * mm, "end": v(1.78, -6.2) * mm});
            skLineSegment(sketch, "E53.3.1", {"start": v(1.78, -6.2) * mm, "end": v(2.97, -6.92) * mm});
            skArc(sketch, "E53.3.2", {"start": v(1.68, -8.17) * mm, "mid": v(2.41, -7.63) * mm, "end": v(2.97, -6.92) * mm});
            skLineSegment(sketch, "E53.3.3", {"start": v(1.01, -6.95) * mm, "end": v(1.68, -8.17) * mm});
            skSolve(sketch);
        }
        {
            var Q0;
            {var subQ0=sQuery(id+"F65.wireOp",EDGE,"E51");Q0=makeQuery(id+"F65.imprint","IMPRINT",FACE,{"disambiguationData":[TD([[makeQuery(id+"F65.imprint","IMPRINT",EDGE,{"derivedFrom":subQ0}),1.0]])]});}
            var Q1;
            {var subQ0=sQuery(id+"F65.wireOp",EDGE,"E49");Q1=makeQuery(id+"F65.imprint","IMPRINT",FACE,{"disambiguationData":[TD([[makeQuery(id+"F65.imprint","IMPRINT",EDGE,{"derivedFrom":subQ0}),-1.0]])]});}
            var Q2;
            {var subQ0=sQuery(id+"F65.wireOp",EDGE,"E53.1.2");Q2=makeQuery(id+"F65.imprint","IMPRINT",FACE,{"disambiguationData":[TD([[makeQuery(id+"F65.imprint","IMPRINT",EDGE,{"derivedFrom":subQ0}),1.0]])]});}
            var Q3;
            {var subQ0=sQuery(id+"F65.wireOp",EDGE,"E53.1.0");Q3=makeQuery(id+"F65.imprint","IMPRINT",FACE,{"disambiguationData":[TD([[makeQuery(id+"F65.imprint","IMPRINT",EDGE,{"derivedFrom":subQ0}),-1.0]])]});}
            var Q4;
            {var subQ0=sQuery(id+"F65.wireOp",EDGE,"E53.2.2");Q4=makeQuery(id+"F65.imprint","IMPRINT",FACE,{"disambiguationData":[TD([[makeQuery(id+"F65.imprint","IMPRINT",EDGE,{"derivedFrom":subQ0}),1.0]])]});}
            var Q5;
            {var subQ0=sQuery(id+"F65.wireOp",EDGE,"E53.2.0");Q5=makeQuery(id+"F65.imprint","IMPRINT",FACE,{"disambiguationData":[TD([[makeQuery(id+"F65.imprint","IMPRINT",EDGE,{"derivedFrom":subQ0}),-1.0]])]});}
            var Q6;
            {var subQ0=sQuery(id+"F65.wireOp",EDGE,"E53.3.2");Q6=makeQuery(id+"F65.imprint","IMPRINT",FACE,{"disambiguationData":[TD([[makeQuery(id+"F65.imprint","IMPRINT",EDGE,{"derivedFrom":subQ0}),1.0]])]});}
            var Q7;
            {var subQ0=sQuery(id+"F65.wireOp",EDGE,"E53.3.0");Q7=makeQuery(id+"F65.imprint","IMPRINT",FACE,{"disambiguationData":[TD([[makeQuery(id+"F65.imprint","IMPRINT",EDGE,{"derivedFrom":subQ0}),-1.0]])]});}
            extrude(context, id + "F66", {"entities" : qUnion([Q0, Q1, Q2, Q3, Q4, Q5, Q6, Q7]), "operationType" : NewBodyOperationType.ADD, "depth" : 2 * mm});
        }
        {
            var Q0;
            Q0=makeQuery(id+"F66.opExtrude","CAP_EDGE",EDGE,{"disambiguationData":[OSD([sQuery(id+"F65.wireOp",EDGE,"E53.1.0")])],"isStart":false});
            chamfer(context, id + "F67", {"entities" : qUnion([Q0]), "width" : 2 * mm, "tangentPropagation" : true});
        }
        {
            var Q0;
            Q0=makeQuery(id+"F66.opExtrude","CAP_EDGE",EDGE,{"disambiguationData":[OSD([sQuery(id+"F65.wireOp",EDGE,"E49")])],"isStart":false});
            var Q1;
            Q1=makeQuery(id+"F66.opExtrude","CAP_EDGE",EDGE,{"disambiguationData":[OSD([sQuery(id+"F65.wireOp",EDGE,"E53.3.0")])],"isStart":false});
            var Q2;
            Q2=makeQuery(id+"F66.opExtrude","CAP_EDGE",EDGE,{"disambiguationData":[OSD([sQuery(id+"F65.wireOp",EDGE,"E53.2.0")])],"isStart":false});
            chamfer(context, id + "F68", {"entities" : qUnion([Q0, Q1, Q2]), "width" : 2 * mm, "tangentPropagation" : true});
        }
        {
            var Q0;
            Q0=makeQuery(id+"F66.opExtrude","CAP_EDGE",EDGE,{"disambiguationData":[OSD([sQuery(id+"F65.wireOp",EDGE,"E53.3.2")])],"isStart":true});
            var Q1;
            Q1=makeQuery(id+"F66.opExtrude","CAP_EDGE",EDGE,{"disambiguationData":[OSD([sQuery(id+"F65.wireOp",EDGE,"E53.2.2")])],"isStart":true});
            var Q2;
            Q2=makeQuery(id+"F66.opExtrude","CAP_EDGE",EDGE,{"disambiguationData":[OSD([sQuery(id+"F65.wireOp",EDGE,"E53.1.2")])],"isStart":true});
            var Q3;
            Q3=makeQuery(id+"F66.opExtrude","CAP_EDGE",EDGE,{"disambiguationData":[OSD([sQuery(id+"F65.wireOp",EDGE,"E51")])],"isStart":true});
            chamfer(context, id + "F69", {"entities" : qUnion([Q0, Q1, Q2, Q3]), "width" : 1 * mm, "tangentPropagation" : true});
        }
        {
            var Q0;
            Q0=makeQuery(id+"F14.opExtrude","CAP_FACE",FACE,{"disambiguationData":[OSD([makeQuery(id+"F12.imprint","IMPRINT",FACE,{"disambiguationData":[TD([[makeQuery(id+"F12.imprint","IMPRINT",EDGE,{"derivedFrom":sQuery(id+"F12.wireOp",EDGE,"E4")}),1.0]])]})])],"isStart":false});
            var sketch = newSketch(context, id + "F70", { "sketchPlane" : qUnion([Q0])});
            skCircle(sketch, "E54", {"center": v(0, 0) * mm, "radius": 3 * mm});
            skSolve(sketch);
        }
        {
            var Q0;
            Q0=makeQuery(id+"F70.imprint","IMPRINT",FACE,{"disambiguationData":[TD([[makeQuery(id+"F70.imprint","IMPRINT",EDGE,{"derivedFrom":sQuery(id+"F70.wireOp",EDGE,"E54")}),1.0]])]});
            extrude(context, id + "F71", {"entities" : qUnion([Q0]), "operationType" : NewBodyOperationType.REMOVE, "oppositeDirection" : true, "depth" : .5 * mm});
        }
        {
            var Q0;
            Q0=qCreatedBy(makeId("Top.planeOp"),FACE);
            var sketch = newSketch(context, id + "F72", { "sketchPlane" : qUnion([Q0])});
            skLineSegment(sketch, "E55", {"start": v(0, 35.25) * mm, "end": v(0, 27.75) * mm});
            skCircle(sketch, "E56", {"center": v(0, 27.75) * mm, "radius": 3.5 * mm});
            skSolve(sketch);
        }
        {
            var Q0;
            Q0 = qSketchRegion(id + "F72", true);
            extrude(context, id + "F73", {"entities" : qUnion([Q0]), "operationType" : NewBodyOperationType.ADD, "depth" : 7.5 * mm});
        }
        {
            var Q0;
            Q0=makeQuery(id+"F73.opExtrude","CAP_FACE",FACE,{"disambiguationData":[OSD([sQuery(id+"F72.wireOp",EDGE,"E56")])],"isStart":false});
            var sketch = newSketch(context, id + "F74", { "sketchPlane" : qUnion([Q0])});
            skCircle(sketch, "E57", {"center": v(0, 27.75) * mm, "radius": 3.25 * mm});
            skSolve(sketch);
        }
        {
            var Q0;
            Q0=makeQuery(id+"F74.imprint","IMPRINT",FACE,{"disambiguationData":[TD([[makeQuery(id+"F74.imprint","IMPRINT",EDGE,{"derivedFrom":sQuery(id+"F74.wireOp",EDGE,"E57")}),1.0]])]});
            extrude(context, id + "F75", {"entities" : qUnion([Q0]), "operationType" : NewBodyOperationType.REMOVE, "oppositeDirection" : true, "depth" : .5 * mm});
        }
    });
